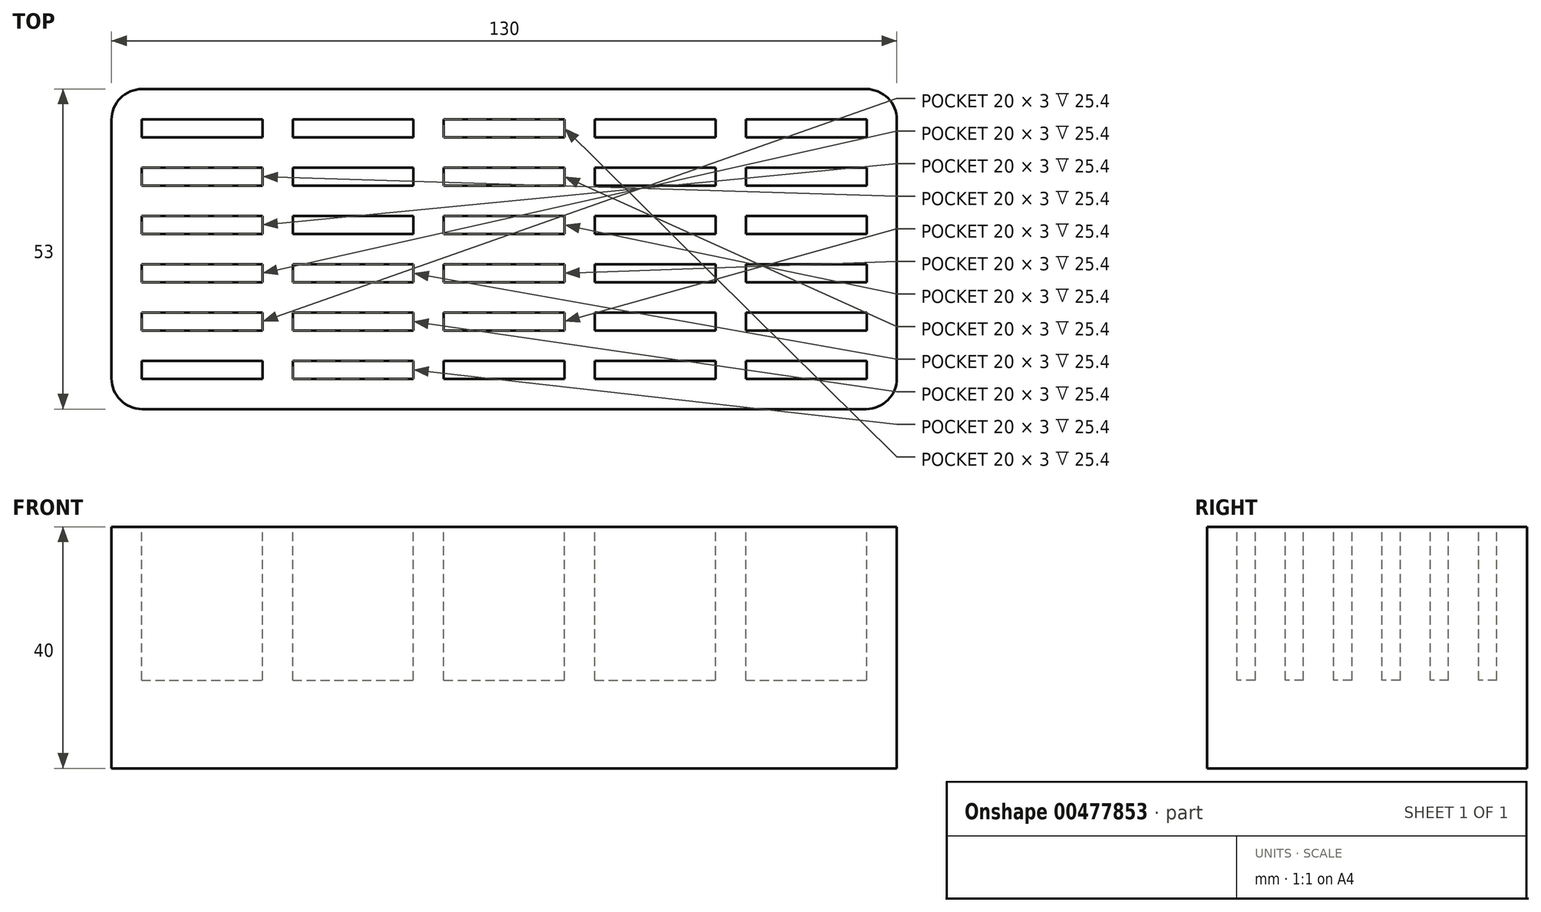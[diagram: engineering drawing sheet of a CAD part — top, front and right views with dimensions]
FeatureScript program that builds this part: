
annotation { "Feature Type Name" : "Feature", "Feature Type Description" : "" }
export const myFeature = defineFeature(function(context is Context, id is Id, definition is map)
    precondition{}
    {
        {
            var Q0;
            Q0=qCreatedBy(makeId("Top.planeOp"),FACE);
            var sketch = newSketch(context, id + "F0", { "sketchPlane" : qUnion([Q0])});
            skLineSegment(sketch, "E0.bottom", {"start": v(5.08, 0) * mm, "end": v(124.92, 0) * mm});
            skLineSegment(sketch, "E0.top", {"start": v(5.08, 53) * mm, "end": v(124.92, 53) * mm});
            skLineSegment(sketch, "E0.left", {"start": v(0, 5.08) * mm, "end": v(0, 47.92) * mm});
            skLineSegment(sketch, "E0.right", {"start": v(130, 5.08) * mm, "end": v(130, 47.92) * mm});
            skPoint(sketch, "E1.visualSharp", {"position": v(0, 53) * mm});
            skArc(sketch, "E1.filletArc", {"start": v(5.08, 53) * mm, "mid": v(1.49, 51.51) * mm, "end": v(0, 47.92) * mm});
            skPoint(sketch, "E2.visualSharp", {"position": v(0, 0) * mm});
            skArc(sketch, "E2.filletArc", {"start": v(0, 5.08) * mm, "mid": v(1.49, 1.49) * mm, "end": v(5.08, 0) * mm});
            skPoint(sketch, "E3.visualSharp", {"position": v(130, 53) * mm});
            skArc(sketch, "E3.filletArc", {"start": v(130, 47.92) * mm, "mid": v(128.51, 51.51) * mm, "end": v(124.92, 53) * mm});
            skPoint(sketch, "E4.visualSharp", {"position": v(130, 0) * mm});
            skArc(sketch, "E4.filletArc", {"start": v(124.92, 0) * mm, "mid": v(128.51, 1.49) * mm, "end": v(130, 5.08) * mm});
            skSolve(sketch);
        }
        {
            var Q0;
            Q0 = qSketchRegion(id + "F0", true);
            extrude(context, id + "F1", {"entities" : qUnion([Q0]), "depth" : 40 * mm});
        }
        {
            var Q0;
            Q0=makeQuery(id+"F1.opExtrude","CAP_FACE",FACE,{"disambiguationData":[OSD([sQuery(id+"F0.wireOp",EDGE,"E0.bottom"),sQuery(id+"F0.wireOp",EDGE,"E0.top"),sQuery(id+"F0.wireOp",EDGE,"E0.left"),sQuery(id+"F0.wireOp",EDGE,"E0.right"),sQuery(id+"F0.wireOp",EDGE,"E1.filletArc"),sQuery(id+"F0.wireOp",EDGE,"E2.filletArc"),sQuery(id+"F0.wireOp",EDGE,"E3.filletArc"),sQuery(id+"F0.wireOp",EDGE,"E4.filletArc")])],"isStart":false});
            var sketch = newSketch(context, id + "F2", { "sketchPlane" : qUnion([Q0])});
            skLineSegment(sketch, "E5.bottom", {"start": v(5, 48) * mm, "end": v(25, 48) * mm});
            skLineSegment(sketch, "E5.top", {"start": v(5, 45) * mm, "end": v(25, 45) * mm});
            skLineSegment(sketch, "E5.left", {"start": v(5, 48) * mm, "end": v(5, 45) * mm});
            skLineSegment(sketch, "E5.right", {"start": v(25, 48) * mm, "end": v(25, 45) * mm});
            skLineSegment(sketch, "E6.0.1.0", {"start": v(5, 40) * mm, "end": v(25, 40) * mm});
            skLineSegment(sketch, "E6.0.1.1", {"start": v(5, 37) * mm, "end": v(25, 37) * mm});
            skLineSegment(sketch, "E6.0.1.2", {"start": v(5, 40) * mm, "end": v(5, 37) * mm});
            skLineSegment(sketch, "E6.0.1.3", {"start": v(25, 40) * mm, "end": v(25, 37) * mm});
            skLineSegment(sketch, "E6.0.2.0", {"start": v(5, 32) * mm, "end": v(25, 32) * mm});
            skLineSegment(sketch, "E6.0.2.1", {"start": v(5, 29) * mm, "end": v(25, 29) * mm});
            skLineSegment(sketch, "E6.0.2.2", {"start": v(5, 32) * mm, "end": v(5, 29) * mm});
            skLineSegment(sketch, "E6.0.2.3", {"start": v(25, 32) * mm, "end": v(25, 29) * mm});
            skLineSegment(sketch, "E6.0.3.0", {"start": v(5, 24) * mm, "end": v(25, 24) * mm});
            skLineSegment(sketch, "E6.0.3.1", {"start": v(5, 21) * mm, "end": v(25, 21) * mm});
            skLineSegment(sketch, "E6.0.3.2", {"start": v(5, 24) * mm, "end": v(5, 21) * mm});
            skLineSegment(sketch, "E6.0.3.3", {"start": v(25, 24) * mm, "end": v(25, 21) * mm});
            skLineSegment(sketch, "E6.0.4.0", {"start": v(5, 16) * mm, "end": v(25, 16) * mm});
            skLineSegment(sketch, "E6.0.4.1", {"start": v(5, 13) * mm, "end": v(25, 13) * mm});
            skLineSegment(sketch, "E6.0.4.2", {"start": v(5, 16) * mm, "end": v(5, 13) * mm});
            skLineSegment(sketch, "E6.0.4.3", {"start": v(25, 16) * mm, "end": v(25, 13) * mm});
            skLineSegment(sketch, "E6.0.5.0", {"start": v(5, 8) * mm, "end": v(25, 8) * mm});
            skLineSegment(sketch, "E6.0.5.1", {"start": v(5, 5) * mm, "end": v(25, 5) * mm});
            skLineSegment(sketch, "E6.0.5.2", {"start": v(5, 8) * mm, "end": v(5, 5) * mm});
            skLineSegment(sketch, "E6.0.5.3", {"start": v(25, 8) * mm, "end": v(25, 5) * mm});
            skLineSegment(sketch, "E6.1.0.0", {"start": v(30, 48) * mm, "end": v(50, 48) * mm});
            skLineSegment(sketch, "E6.1.0.1", {"start": v(30, 45) * mm, "end": v(50, 45) * mm});
            skLineSegment(sketch, "E6.1.0.2", {"start": v(30, 48) * mm, "end": v(30, 45) * mm});
            skLineSegment(sketch, "E6.1.0.3", {"start": v(50, 48) * mm, "end": v(50, 45) * mm});
            skLineSegment(sketch, "E6.1.1.0", {"start": v(30, 40) * mm, "end": v(50, 40) * mm});
            skLineSegment(sketch, "E6.1.1.1", {"start": v(30, 37) * mm, "end": v(50, 37) * mm});
            skLineSegment(sketch, "E6.1.1.2", {"start": v(30, 40) * mm, "end": v(30, 37) * mm});
            skLineSegment(sketch, "E6.1.1.3", {"start": v(50, 40) * mm, "end": v(50, 37) * mm});
            skLineSegment(sketch, "E6.1.2.0", {"start": v(30, 32) * mm, "end": v(50, 32) * mm});
            skLineSegment(sketch, "E6.1.2.1", {"start": v(30, 29) * mm, "end": v(50, 29) * mm});
            skLineSegment(sketch, "E6.1.2.2", {"start": v(30, 32) * mm, "end": v(30, 29) * mm});
            skLineSegment(sketch, "E6.1.2.3", {"start": v(50, 32) * mm, "end": v(50, 29) * mm});
            skLineSegment(sketch, "E6.1.3.0", {"start": v(30, 24) * mm, "end": v(50, 24) * mm});
            skLineSegment(sketch, "E6.1.3.1", {"start": v(30, 21) * mm, "end": v(50, 21) * mm});
            skLineSegment(sketch, "E6.1.3.2", {"start": v(30, 24) * mm, "end": v(30, 21) * mm});
            skLineSegment(sketch, "E6.1.3.3", {"start": v(50, 24) * mm, "end": v(50, 21) * mm});
            skLineSegment(sketch, "E6.1.4.0", {"start": v(30, 16) * mm, "end": v(50, 16) * mm});
            skLineSegment(sketch, "E6.1.4.1", {"start": v(30, 13) * mm, "end": v(50, 13) * mm});
            skLineSegment(sketch, "E6.1.4.2", {"start": v(30, 16) * mm, "end": v(30, 13) * mm});
            skLineSegment(sketch, "E6.1.4.3", {"start": v(50, 16) * mm, "end": v(50, 13) * mm});
            skLineSegment(sketch, "E6.1.5.0", {"start": v(30, 8) * mm, "end": v(50, 8) * mm});
            skLineSegment(sketch, "E6.1.5.1", {"start": v(30, 5) * mm, "end": v(50, 5) * mm});
            skLineSegment(sketch, "E6.1.5.2", {"start": v(30, 8) * mm, "end": v(30, 5) * mm});
            skLineSegment(sketch, "E6.1.5.3", {"start": v(50, 8) * mm, "end": v(50, 5) * mm});
            skLineSegment(sketch, "E6.2.0.0", {"start": v(55, 48) * mm, "end": v(75, 48) * mm});
            skLineSegment(sketch, "E6.2.0.1", {"start": v(55, 45) * mm, "end": v(75, 45) * mm});
            skLineSegment(sketch, "E6.2.0.2", {"start": v(55, 48) * mm, "end": v(55, 45) * mm});
            skLineSegment(sketch, "E6.2.0.3", {"start": v(75, 48) * mm, "end": v(75, 45) * mm});
            skLineSegment(sketch, "E6.2.1.0", {"start": v(55, 40) * mm, "end": v(75, 40) * mm});
            skLineSegment(sketch, "E6.2.1.1", {"start": v(55, 37) * mm, "end": v(75, 37) * mm});
            skLineSegment(sketch, "E6.2.1.2", {"start": v(55, 40) * mm, "end": v(55, 37) * mm});
            skLineSegment(sketch, "E6.2.1.3", {"start": v(75, 40) * mm, "end": v(75, 37) * mm});
            skLineSegment(sketch, "E6.2.2.0", {"start": v(55, 32) * mm, "end": v(75, 32) * mm});
            skLineSegment(sketch, "E6.2.2.1", {"start": v(55, 29) * mm, "end": v(75, 29) * mm});
            skLineSegment(sketch, "E6.2.2.2", {"start": v(55, 32) * mm, "end": v(55, 29) * mm});
            skLineSegment(sketch, "E6.2.2.3", {"start": v(75, 32) * mm, "end": v(75, 29) * mm});
            skLineSegment(sketch, "E6.2.3.0", {"start": v(55, 24) * mm, "end": v(75, 24) * mm});
            skLineSegment(sketch, "E6.2.3.1", {"start": v(55, 21) * mm, "end": v(75, 21) * mm});
            skLineSegment(sketch, "E6.2.3.2", {"start": v(55, 24) * mm, "end": v(55, 21) * mm});
            skLineSegment(sketch, "E6.2.3.3", {"start": v(75, 24) * mm, "end": v(75, 21) * mm});
            skLineSegment(sketch, "E6.2.4.0", {"start": v(55, 16) * mm, "end": v(75, 16) * mm});
            skLineSegment(sketch, "E6.2.4.1", {"start": v(55, 13) * mm, "end": v(75, 13) * mm});
            skLineSegment(sketch, "E6.2.4.2", {"start": v(55, 16) * mm, "end": v(55, 13) * mm});
            skLineSegment(sketch, "E6.2.4.3", {"start": v(75, 16) * mm, "end": v(75, 13) * mm});
            skLineSegment(sketch, "E6.2.5.0", {"start": v(55, 8) * mm, "end": v(75, 8) * mm});
            skLineSegment(sketch, "E6.2.5.1", {"start": v(55, 5) * mm, "end": v(75, 5) * mm});
            skLineSegment(sketch, "E6.2.5.2", {"start": v(55, 8) * mm, "end": v(55, 5) * mm});
            skLineSegment(sketch, "E6.2.5.3", {"start": v(75, 8) * mm, "end": v(75, 5) * mm});
            skLineSegment(sketch, "E6.3.0.0", {"start": v(80, 48) * mm, "end": v(100, 48) * mm});
            skLineSegment(sketch, "E6.3.0.1", {"start": v(80, 45) * mm, "end": v(100, 45) * mm});
            skLineSegment(sketch, "E6.3.0.2", {"start": v(80, 48) * mm, "end": v(80, 45) * mm});
            skLineSegment(sketch, "E6.3.0.3", {"start": v(100, 48) * mm, "end": v(100, 45) * mm});
            skLineSegment(sketch, "E6.3.1.0", {"start": v(80, 40) * mm, "end": v(100, 40) * mm});
            skLineSegment(sketch, "E6.3.1.1", {"start": v(80, 37) * mm, "end": v(100, 37) * mm});
            skLineSegment(sketch, "E6.3.1.2", {"start": v(80, 40) * mm, "end": v(80, 37) * mm});
            skLineSegment(sketch, "E6.3.1.3", {"start": v(100, 40) * mm, "end": v(100, 37) * mm});
            skLineSegment(sketch, "E6.3.2.0", {"start": v(80, 32) * mm, "end": v(100, 32) * mm});
            skLineSegment(sketch, "E6.3.2.1", {"start": v(80, 29) * mm, "end": v(100, 29) * mm});
            skLineSegment(sketch, "E6.3.2.2", {"start": v(80, 32) * mm, "end": v(80, 29) * mm});
            skLineSegment(sketch, "E6.3.2.3", {"start": v(100, 32) * mm, "end": v(100, 29) * mm});
            skLineSegment(sketch, "E6.3.3.0", {"start": v(80, 24) * mm, "end": v(100, 24) * mm});
            skLineSegment(sketch, "E6.3.3.1", {"start": v(80, 21) * mm, "end": v(100, 21) * mm});
            skLineSegment(sketch, "E6.3.3.2", {"start": v(80, 24) * mm, "end": v(80, 21) * mm});
            skLineSegment(sketch, "E6.3.3.3", {"start": v(100, 24) * mm, "end": v(100, 21) * mm});
            skLineSegment(sketch, "E6.3.4.0", {"start": v(80, 16) * mm, "end": v(100, 16) * mm});
            skLineSegment(sketch, "E6.3.4.1", {"start": v(80, 13) * mm, "end": v(100, 13) * mm});
            skLineSegment(sketch, "E6.3.4.2", {"start": v(80, 16) * mm, "end": v(80, 13) * mm});
            skLineSegment(sketch, "E6.3.4.3", {"start": v(100, 16) * mm, "end": v(100, 13) * mm});
            skLineSegment(sketch, "E6.3.5.0", {"start": v(80, 8) * mm, "end": v(100, 8) * mm});
            skLineSegment(sketch, "E6.3.5.1", {"start": v(80, 5) * mm, "end": v(100, 5) * mm});
            skLineSegment(sketch, "E6.3.5.2", {"start": v(80, 8) * mm, "end": v(80, 5) * mm});
            skLineSegment(sketch, "E6.3.5.3", {"start": v(100, 8) * mm, "end": v(100, 5) * mm});
            skLineSegment(sketch, "E6.4.0.0", {"start": v(105, 48) * mm, "end": v(125, 48) * mm});
            skLineSegment(sketch, "E6.4.0.1", {"start": v(105, 45) * mm, "end": v(125, 45) * mm});
            skLineSegment(sketch, "E6.4.0.2", {"start": v(105, 48) * mm, "end": v(105, 45) * mm});
            skLineSegment(sketch, "E6.4.0.3", {"start": v(125, 48) * mm, "end": v(125, 45) * mm});
            skLineSegment(sketch, "E6.4.1.0", {"start": v(105, 40) * mm, "end": v(125, 40) * mm});
            skLineSegment(sketch, "E6.4.1.1", {"start": v(105, 37) * mm, "end": v(125, 37) * mm});
            skLineSegment(sketch, "E6.4.1.2", {"start": v(105, 40) * mm, "end": v(105, 37) * mm});
            skLineSegment(sketch, "E6.4.1.3", {"start": v(125, 40) * mm, "end": v(125, 37) * mm});
            skLineSegment(sketch, "E6.4.2.0", {"start": v(105, 32) * mm, "end": v(125, 32) * mm});
            skLineSegment(sketch, "E6.4.2.1", {"start": v(105, 29) * mm, "end": v(125, 29) * mm});
            skLineSegment(sketch, "E6.4.2.2", {"start": v(105, 32) * mm, "end": v(105, 29) * mm});
            skLineSegment(sketch, "E6.4.2.3", {"start": v(125, 32) * mm, "end": v(125, 29) * mm});
            skLineSegment(sketch, "E6.4.3.0", {"start": v(105, 24) * mm, "end": v(125, 24) * mm});
            skLineSegment(sketch, "E6.4.3.1", {"start": v(105, 21) * mm, "end": v(125, 21) * mm});
            skLineSegment(sketch, "E6.4.3.2", {"start": v(105, 24) * mm, "end": v(105, 21) * mm});
            skLineSegment(sketch, "E6.4.3.3", {"start": v(125, 24) * mm, "end": v(125, 21) * mm});
            skLineSegment(sketch, "E6.4.4.0", {"start": v(105, 16) * mm, "end": v(125, 16) * mm});
            skLineSegment(sketch, "E6.4.4.1", {"start": v(105, 13) * mm, "end": v(125, 13) * mm});
            skLineSegment(sketch, "E6.4.4.2", {"start": v(105, 16) * mm, "end": v(105, 13) * mm});
            skLineSegment(sketch, "E6.4.4.3", {"start": v(125, 16) * mm, "end": v(125, 13) * mm});
            skLineSegment(sketch, "E6.4.5.0", {"start": v(105, 8) * mm, "end": v(125, 8) * mm});
            skLineSegment(sketch, "E6.4.5.1", {"start": v(105, 5) * mm, "end": v(125, 5) * mm});
            skLineSegment(sketch, "E6.4.5.2", {"start": v(105, 8) * mm, "end": v(105, 5) * mm});
            skLineSegment(sketch, "E6.4.5.3", {"start": v(125, 8) * mm, "end": v(125, 5) * mm});
            skLineSegment(sketch, "E6.direction1", {"start": v(5, 48) * mm, "end": v(30, 48) * mm, "construction": true});
            skLineSegment(sketch, "E6.direction2", {"start": v(5, 48) * mm, "end": v(5, 40) * mm, "construction": true});
            skSolve(sketch);
        }
        {
            var Q0;
            Q0 = qSketchRegion(id + "F2", true);
            extrude(context, id + "F3", {"entities" : qUnion([Q0]), "operationType" : NewBodyOperationType.REMOVE, "oppositeDirection" : true, "depth" : 25.4 * mm});
        }
    });
